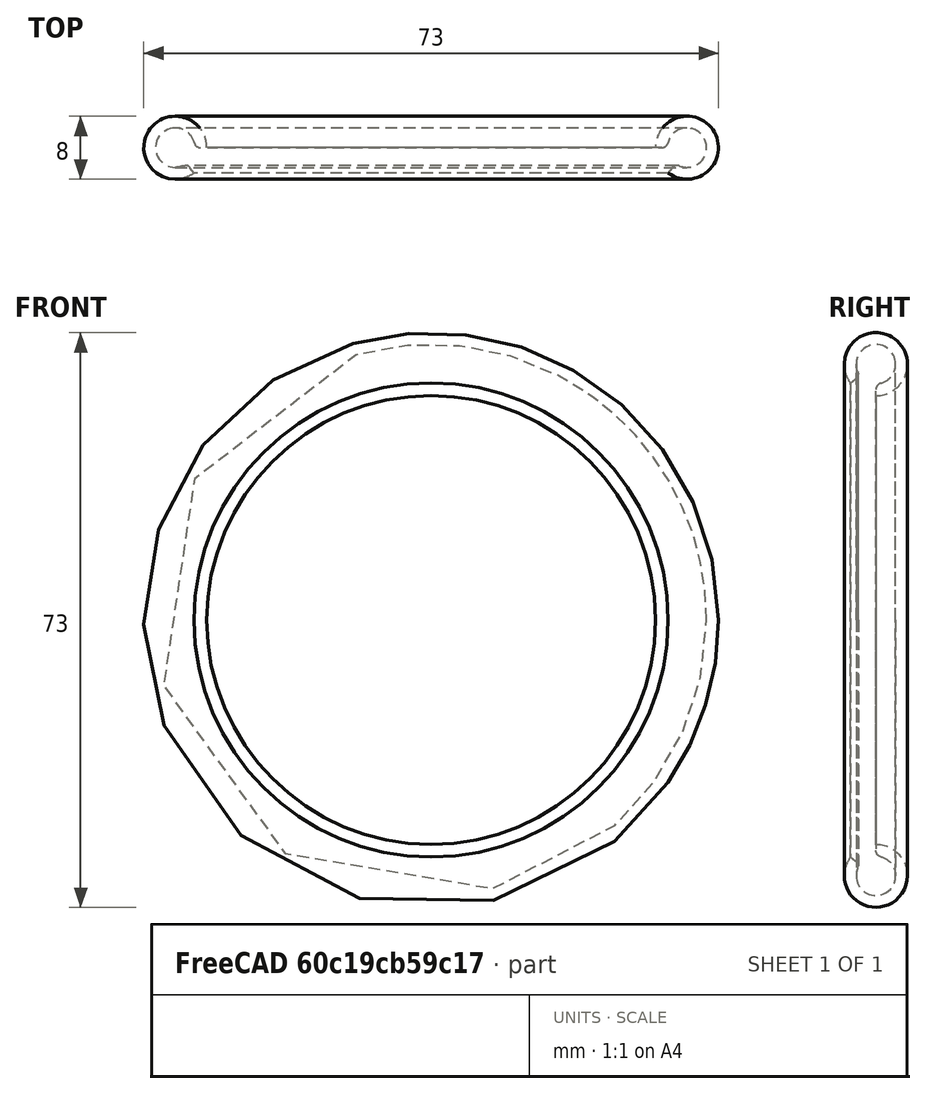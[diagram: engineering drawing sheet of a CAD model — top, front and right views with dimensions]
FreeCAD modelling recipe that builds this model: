
FCSTD DOCUMENT  (FreeCAD 0.15R4671 (Git))
Label: Kraken
License: All rights reserved
LicenseURL: http://en.wikipedia.org/wiki/All_rights_reserved
objects: Sketcher::SketchObject×3, App::MeasureDistance×2, Mesh::Feature×1, Part::Sweep×1
note: 4 computed .brp shape members not serialized (recipe doc carries the construction recipe); baked Part::Feature solids carry a one-line shape summary decoded from their .brp

FEATURE [Sketcher::SketchObject] Sketch
  Placement = pos=(0,0,0) rot=(1,0,0;1.5708rad)
  sketch-geometry (1):
    g0: Circle CenterX=0 CenterY=0 CenterZ=0 NormalX=0 NormalY=0 NormalZ=1 Radius=33.0454
  constraints (1):
    c: Coincident(g0,g-1)
FEATURE [Sketcher::SketchObject] Sketch001
  sketch-geometry (8):
    g0: ArcOfCircle CenterX=-32.5 CenterY=0 CenterZ=0 NormalX=0 NormalY=0 NormalZ=1 Radius=4 StartAngle=0.00156416 EndAngle=5.35226
    g1: ArcOfCircle CenterX=-32.5 CenterY=0 CenterZ=0 NormalX=0 NormalY=0 NormalZ=1 Radius=2.5 StartAngle=0.246818 EndAngle=5.10701
    g2: ArcOfCircle CenterX=-31.2313 CenterY=-3.04637 CenterZ=0 NormalX=0 NormalY=0 NormalZ=1 Radius=0.8 StartAngle=0.641434 EndAngle=1.96541
    g3: ArcOfCircle CenterX=-29.3 CenterY=0.806257 CenterZ=0 NormalX=0 NormalY=0 NormalZ=1 Radius=0.8 StartAngle=3.38841 EndAngle=4.71239
    g4: LineSegment StartX=-28.5 StartY=0.00625665 StartZ=0 EndX=-29.3 EndY=0.00625665 EndZ=0
    g5: LineSegment StartX=-30.5903 StartY=-2.5677 StartZ=0 EndX=-30.1116 EndY=-3.20869 EndZ=0
    g6: LineSegment [constr] StartX=-32.5 StartY=0 StartZ=0 EndX=-29.3 EndY=0.00625665 EndZ=0
    g7: LineSegment [constr] StartX=-32.5 StartY=0 StartZ=0 EndX=-30.5903 EndY=-2.5677 EndZ=0
  constraints (25):
    c: Coincident(g1,g0)
    c: Radius(g1) = 2.5
    c: Radius(g0) = 4
    c: Coincident(g2,g1)
    c: Coincident(g3,g1)
    c: Radius(g3) = 0.8
    c: Radius(g2) = 0.8
    c: Coincident(g4,g0)
    c: Coincident(g4,g3)
    c: Horizontal(g4)
    c: Coincident(g5,g2)
    c: Coincident(g5,g0)
    c: Tangent(g2,g1)
    c: Tangent(g3,g1)
    c: Tangent(g3,g4)
    c: Tangent(g2,g5)
    c: Distance(g4) = 0.8
    c: Distance(g5) = 0.8
    c: Coincident(g6,g0)
    c: Coincident(g6,g3)
    c: Coincident(g7,g2)
    c: Coincident(g7,g0)
    c: Angle(g7,g6) = 0.933269
    c: PointOnObject(g0,g-1)
    c: DistanceX(g-2,g0) = -32.5
FEATURE [Mesh::Feature] Kraken_tans
  Placement = pos=(-0.116232,15.0906,-0.155784) rot=(0,0,1;0rad)
FEATURE [Part::Sweep] Sweep
  Frenet = false
  Sections = -> [Sketch001]
  Solid = false
  Spine = -> Sketch [Edge1]
  Transition = 1
FEATURE [Sketcher::SketchObject] Sketch002
  Placement = pos=(0,0,0) rot=(0,0.707107,0.707107;3.14159rad)
  sketch-geometry (4):
    g0: LineSegment StartX=-14.8639 StartY=14.8413 StartZ=0 EndX=15.1361 EndY=14.8413 EndZ=0
    g1: LineSegment StartX=15.1361 StartY=14.8413 StartZ=0 EndX=15.1361 EndY=-15.1587 EndZ=0
    g2: LineSegment StartX=15.1361 StartY=-15.1587 StartZ=0 EndX=-14.8639 EndY=-15.1587 EndZ=0
    g3: LineSegment StartX=-14.8639 StartY=-15.1587 StartZ=0 EndX=-14.8639 EndY=14.8413 EndZ=0
  constraints (10):
    c: Coincident(g0,g1)
    c: Coincident(g1,g2)
    c: Coincident(g2,g3)
    c: Coincident(g3,g0)
    c: Horizontal(g0)
    c: Horizontal(g2)
    c: Vertical(g1)
    c: Vertical(g3)
    c: Distance(g0) = 30
    c: Distance(g1) = 30
FEATURE [App::MeasureDistance] Distance  label="Distance: 39.863"
  Distance = 39.8628
  P1 = (86.1991,47.3531,19.6177)
  P2 = (83.8134,46.1635,-20.1558)
FEATURE [App::MeasureDistance] Distance001  label="Distance: 28.800"
  Distance = 28.8003
  P1 = (63.3638,28.9789,-20.1558)
  P2 = (88.0968,43.7349,-20.1558)
